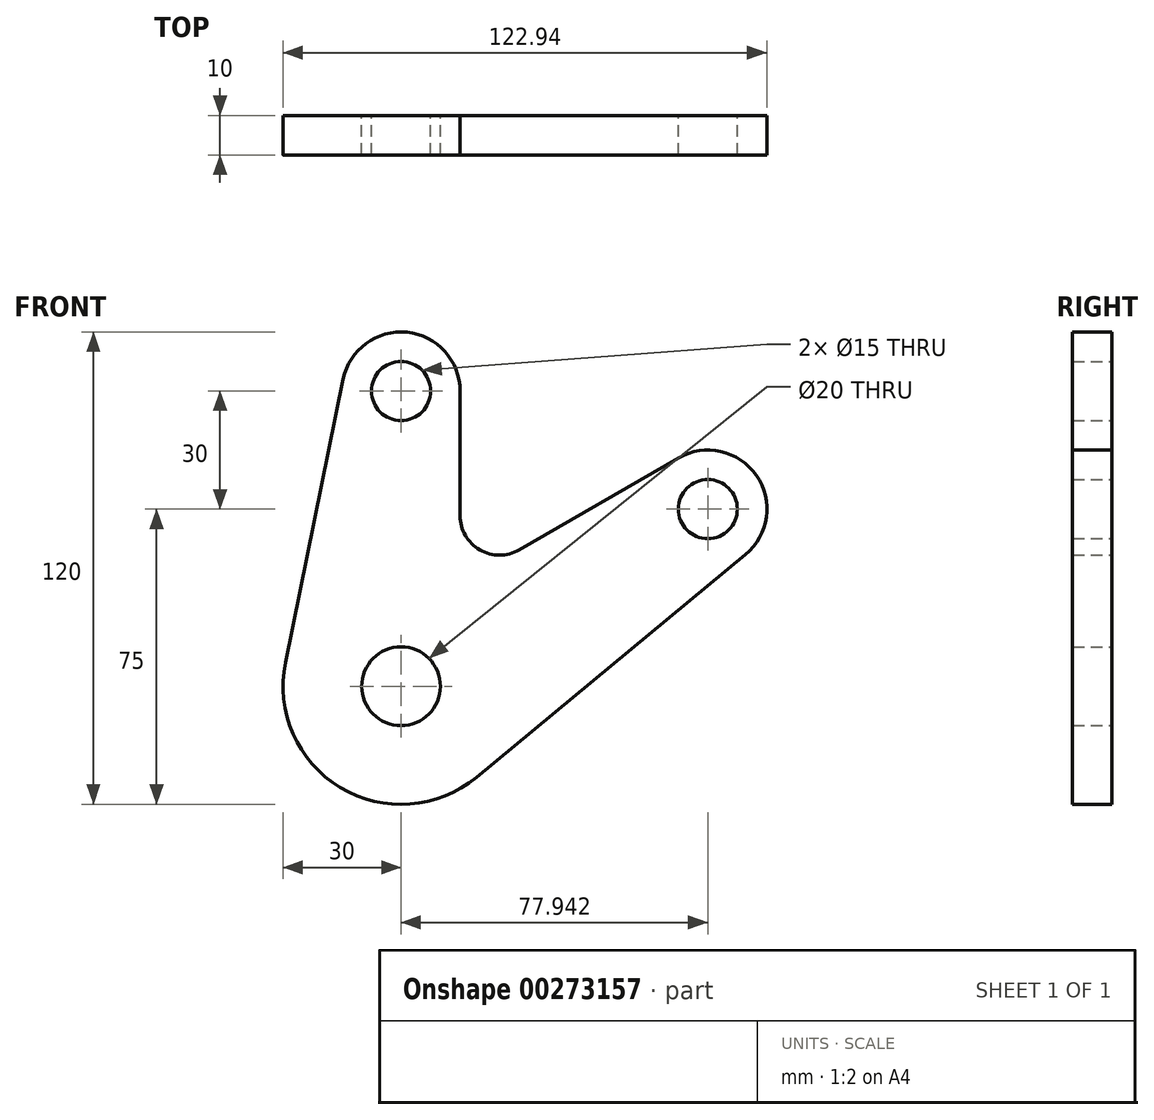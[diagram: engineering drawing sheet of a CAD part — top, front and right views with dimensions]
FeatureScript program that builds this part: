
annotation { "Feature Type Name" : "Feature", "Feature Type Description" : "" }
export const myFeature = defineFeature(function(context is Context, id is Id, definition is map)
    precondition{}
    {
        {
            var Q0;
            Q0=qCreatedBy(makeId("Front.planeOp"),FACE);
            var sketch = newSketch(context, id + "F0", { "sketchPlane" : qUnion([Q0])});
            skLineSegment(sketch, "E0", {"start": v(0, 0) * mm, "end": v(0, 75) * mm, "construction": true});
            skLineSegment(sketch, "E1", {"start": v(0, 0) * mm, "end": v(77.94, 45) * mm, "construction": true});
            skLineSegment(sketch, "E2", {"start": v(15, 75) * mm, "end": v(15, 43.3) * mm});
            skLineSegment(sketch, "E3", {"start": v(30, 34.64) * mm, "end": v(70.44, 58) * mm});
            skArc(sketch, "E4", {"start": v(15, 43.3) * mm, "mid": v(20, 34.64) * mm, "end": v(30, 34.64) * mm});
            skLineSegment(sketch, "E5", {"start": v(-14.7, 78) * mm, "end": v(-29.4, 6) * mm});
            skLineSegment(sketch, "E6", {"start": v(19.12, -23.12) * mm, "end": v(87.5, 33.44) * mm});
            skArc(sketch, "E7", {"start": v(-14.7, 78) * mm, "mid": v(1.5, 89.92) * mm, "end": v(15, 75) * mm});
            skArc(sketch, "E8", {"start": v(-29.4, 6) * mm, "mid": v(-15.44, -25.72) * mm, "end": v(19.12, -23.12) * mm});
            skArc(sketch, "E9", {"start": v(87.5, 33.44) * mm, "mid": v(90.26, 53.56) * mm, "end": v(70.44, 58) * mm});
            skCircle(sketch, "E10", {"center": v(0, 0) * mm, "radius": 10 * mm});
            skCircle(sketch, "E11", {"center": v(0, 75) * mm, "radius": 7.5 * mm});
            skCircle(sketch, "E12", {"center": v(77.94, 45) * mm, "radius": 7.5 * mm});
            skSolve(sketch);
        }
        {
            var Q0;
            Q0=makeQuery(id+"F0.imprint","IMPRINT",FACE,{"disambiguationData":[TD([[makeQuery(id+"F0.imprint","IMPRINT",EDGE,{"derivedFrom":sQuery(id+"F0.wireOp",EDGE,"E2")}),-1.0]])]});
            extrude(context, id + "F1", {"entities" : qUnion([Q0]), "depth" : 10 * mm});
        }
    });
